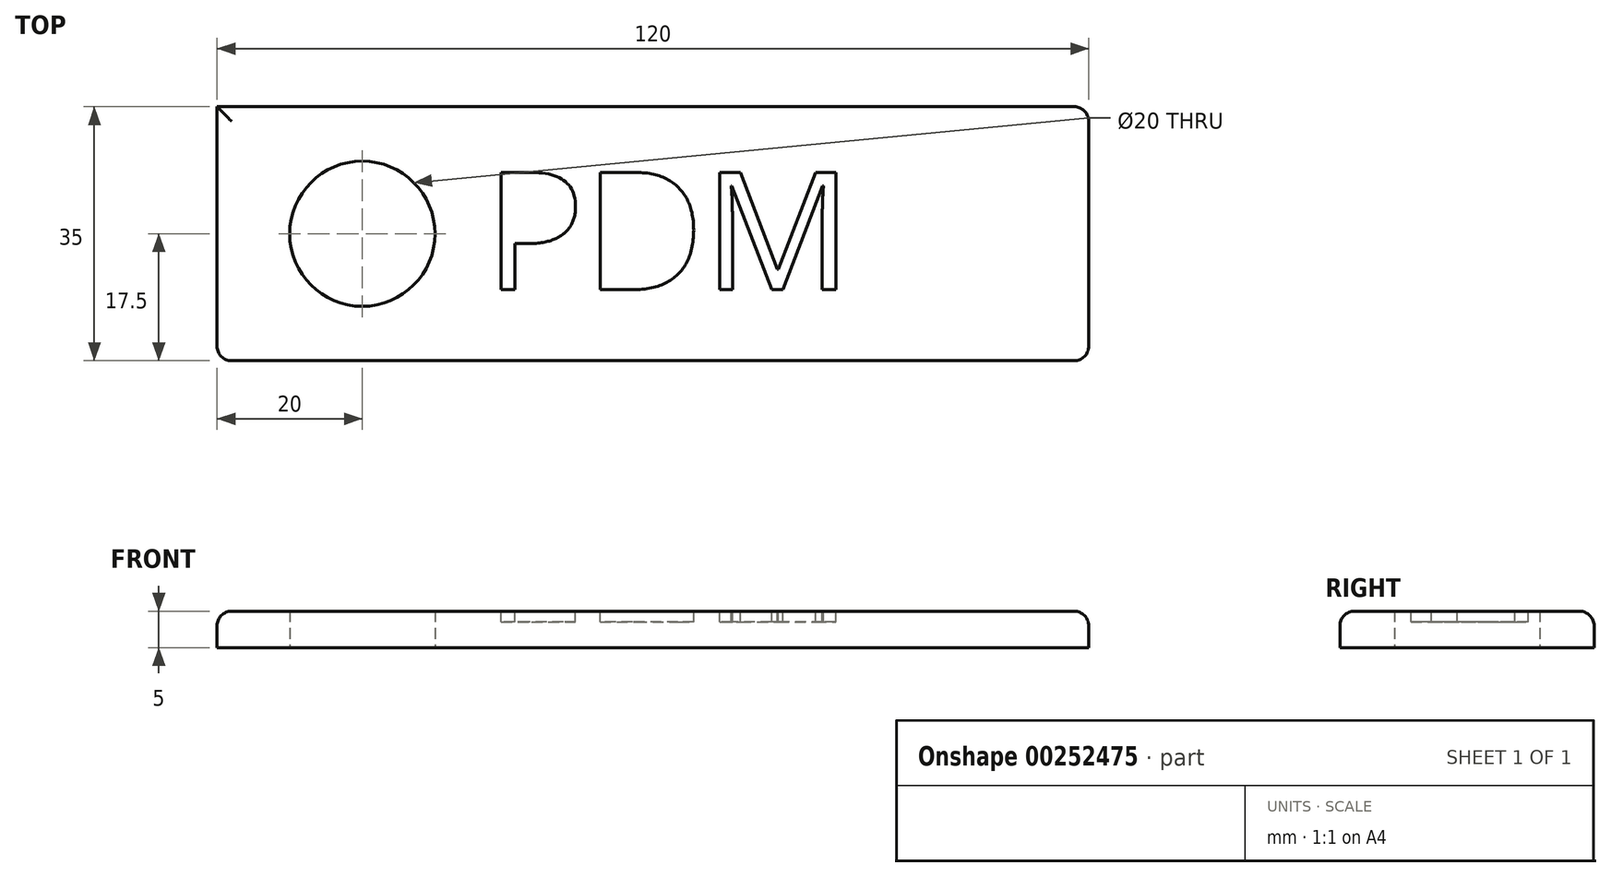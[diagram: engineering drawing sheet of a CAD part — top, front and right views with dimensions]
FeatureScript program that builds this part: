
annotation { "Feature Type Name" : "Feature", "Feature Type Description" : "" }
export const myFeature = defineFeature(function(context is Context, id is Id, definition is map)
    precondition{}
    {
        {
            var Q0;
            Q0=qCreatedBy(makeId("Top.planeOp"),FACE);
            var sketch = newSketch(context, id + "F0", { "sketchPlane" : qUnion([Q0])});
            skLineSegment(sketch, "E0.bottom", {"start": v(60, -17.5) * mm, "end": v(-60, -17.5) * mm});
            skLineSegment(sketch, "E0.top", {"start": v(60, 17.5) * mm, "end": v(-60, 17.5) * mm});
            skLineSegment(sketch, "E0.left", {"start": v(60, -17.5) * mm, "end": v(60, 17.5) * mm});
            skLineSegment(sketch, "E0.right", {"start": v(-60, -17.5) * mm, "end": v(-60, 17.5) * mm});
            skPoint(sketch, "E0.middle", {"position": v(0, 0) * mm});
            skCircle(sketch, "E1", {"center": v(-40, 0) * mm, "radius": 10 * mm});
            skSolve(sketch);
        }
        {
            var Q0;
            Q0=makeQuery(id+"F0.imprint","IMPRINT",FACE,{"disambiguationData":[TD([[makeQuery(id+"F0.imprint","IMPRINT",EDGE,{"derivedFrom":sQuery(id+"F0.wireOp",EDGE,"E0.bottom")}),-1.0]])]});
            extrude(context, id + "F1", {"entities" : qUnion([Q0]), "depth" : 5 * mm});
        }
        {
            var Q0;
            Q0=makeQuery(id+"F1.opExtrude","CAP_EDGE",EDGE,{"disambiguationData":[OSD([sQuery(id+"F0.wireOp",EDGE,"E0.bottom")])],"isStart":false});
            fillet(context, id + "F2", {"entities" : qUnion([Q0]), "radius" : 2 * mm, "tangentPropagation" : true, "allowEdgeOverflow" : false});
        }
        {
            var Q0;
            Q0=makeQuery(id+"F1.opExtrude","CAP_EDGE",EDGE,{"disambiguationData":[OSD([sQuery(id+"F0.wireOp",EDGE,"E0.left")])],"isStart":false});
            fillet(context, id + "F3", {"entities" : qUnion([Q0]), "radius" : 2 * mm, "tangentPropagation" : true, "allowEdgeOverflow" : false});
        }
        {
            var Q0;
            Q0=makeQuery(id+"F1.opExtrude","CAP_EDGE",EDGE,{"disambiguationData":[OSD([sQuery(id+"F0.wireOp",EDGE,"E0.top")])],"isStart":false});
            var Q1;
            Q1=makeQuery(id+"F1.opExtrude","CAP_EDGE",EDGE,{"disambiguationData":[OSD([sQuery(id+"F0.wireOp",EDGE,"E0.right")])],"isStart":false});
            fillet(context, id + "F4", {"entities" : qUnion([Q0, Q1]), "radius" : 2 * mm, "tangentPropagation" : true, "allowEdgeOverflow" : false});
        }
        {
            var Q0;
            Q0=makeQuery(id+"F1.opExtrude","CAP_FACE",FACE,{"disambiguationData":[OSD([sQuery(id+"F0.wireOp",EDGE,"E0.bottom"),sQuery(id+"F0.wireOp",EDGE,"E0.top"),sQuery(id+"F0.wireOp",EDGE,"E0.left"),sQuery(id+"F0.wireOp",EDGE,"E0.right"),sQuery(id+"F0.wireOp",EDGE,"E1")])],"isStart":false});
            var sketch = newSketch(context, id + "F5", { "sketchPlane" : qUnion([Q0])});
            skText(sketch, "E2", { "text": "PDM", "fontName": "OpenSans-Regular.ttf"});
            skFitSpline(sketch, "E3", {"points": [v(41.45, 9.47) * mm, v(36.12, 8) * mm, v(32.27, 3.55) * mm, v(31.68, 0) * mm, v(33.45, -3.26) * mm, v(36.71, -5.92) * mm, v(41.45, -6.8) * mm], "startDerivative": vector(-30.43, -4.05) * mm, "endDerivative": vector(29.35, -2.37) * mm});
            skFitSpline(sketch, "E4.MirrorCS", {"points": [v(41.45, 9.47) * mm, v(46.78, 8) * mm, v(50.63, 3.55) * mm, v(51.22, 0) * mm, v(49.44, -3.26) * mm, v(46.18, -5.92) * mm, v(41.45, -6.8) * mm], "startDerivative": vector(30.43, -4.05) * mm, "endDerivative": vector(-29.35, -2.37) * mm});
            const initialGuessF5  = {"E2": [-0.0231, -0.0077, 1, 0, 0.01628]};
            skSetInitialGuess(sketch, initialGuessF5);
            skSolve(sketch);
        }
        {
            var Q0;
            Q0=makeQuery(id+"F5.imprint","IMPRINT",FACE,{"disambiguationData":[TD([[makeQuery(id+"F5.imprint","IMPRINT",EDGE,{"derivedFrom":sQuery(id+"F5.wireOp",EDGE,"E2.sketch_text.stroke-0")}),1.0]])]});
            var sketch = newSketch(context, id + "F6", { "sketchPlane" : qUnion([Q0])});
            skLineSegment(sketch, "E5", {"start": v(41.15, 5.33) * mm, "end": v(41.15, -3.55) * mm});
            skSolve(sketch);
        }
        {
            var Q0;
            Q0 = qSketchRegion(id + "F5", true);
            extrude(context, id + "F7", {"entities" : qUnion([Q0]), "operationType" : NewBodyOperationType.ADD, "oppositeDirection" : true, "depth" : 1.5 * mm});
        }
        {
            var Q0;
            Q0=makeQuery(id+"F6.imprint","IMPRINT",FACE,{"disambiguationData":[TD([[makeQuery(id+"F6.imprint","IMPRINT",EDGE,{"derivedFrom":makeQuery(id+"F5.imprint","IMPRINT",EDGE,{"derivedFrom":sQuery(id+"F5.wireOp",EDGE,"E2.sketch_text.stroke-0")})}),-1.0]])]});
            var Q1;
            Q1=makeQuery(id+"F6.imprint","IMPRINT",FACE,{"disambiguationData":[TD([[makeQuery(id+"F6.imprint","IMPRINT",EDGE,{"derivedFrom":makeQuery(id+"F5.imprint","IMPRINT",EDGE,{"derivedFrom":sQuery(id+"F5.wireOp",EDGE,"E2.sketch_text.stroke-15")})}),-1.0]])]});
            var Q2;
            Q2=makeQuery(id+"F6.imprint","IMPRINT",FACE,{"disambiguationData":[TD([[makeQuery(id+"F6.imprint","IMPRINT",EDGE,{"derivedFrom":makeQuery(id+"F5.imprint","IMPRINT",EDGE,{"derivedFrom":sQuery(id+"F5.wireOp",EDGE,"E2.sketch_text.stroke-29")})}),-1.0]])]});
            extrude(context, id + "F8", {"entities" : qUnion([Q0, Q1, Q2]), "operationType" : NewBodyOperationType.REMOVE, "oppositeDirection" : true, "depth" : 1.5 * mm});
        }
        {
            var Q0;
            Q0=sQuery(id+"F5.wireOp",EDGE,"E4.MirrorCS");
            var Q1;
            Q1=sQuery(id+"F5.wireOp",EDGE,"E3");
            extrude(context, id + "F9", {"bodyType" : ToolBodyType.SURFACE, "surfaceEntities" : qUnion([Q0, Q1]), "oppositeDirection" : true, "depth" : 1.5 * mm});
        }
        {
            var Q0;
            Q0=sQuery(id+"F6.wireOp",EDGE,"E5");
            extrude(context, id + "F10", {"bodyType" : ToolBodyType.SURFACE, "surfaceEntities" : qUnion([Q0]), "oppositeDirection" : true, "depth" : 1.5 * mm});
        }
    });
